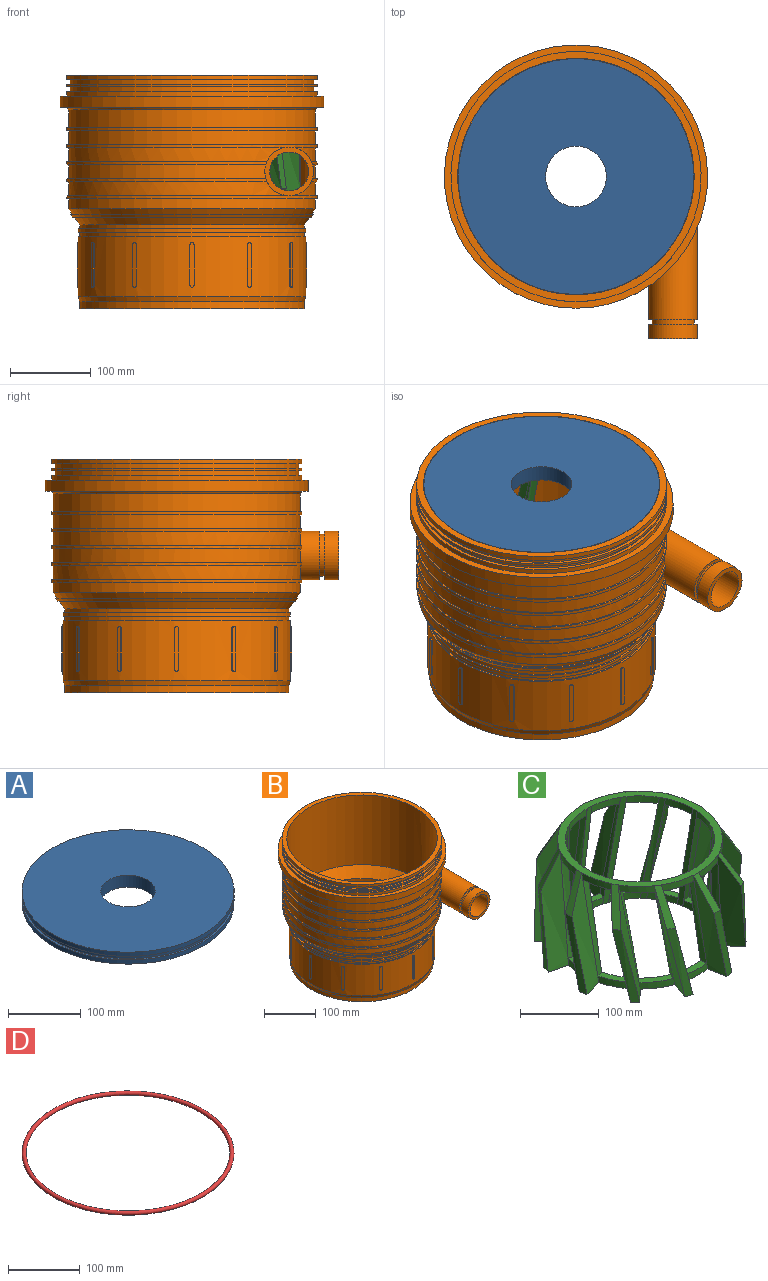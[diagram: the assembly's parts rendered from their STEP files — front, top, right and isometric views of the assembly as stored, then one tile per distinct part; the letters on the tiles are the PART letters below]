
ASSEMBLY  parts=4 mates=3
PART A: 8 faces, bbox 292x292x20 mm
  f0: cylinder r=146mm len=292mm, axis (0,0,-1), area 6421.4mm2, adj f1,f2
  f1: plane 292x292mm, normal (0,0,1), area 2723.8mm2, adj f0,f3
  f2: plane 292x292mm, normal (0,0,-1), area 62548.3mm2, adj f0,f7
  f3: cylinder r=143mm len=286mm, axis (0,0,-1), area 5391mm2, adj f1,f6
  f4: cylinder r=146mm len=292mm, axis (0,0,-1), area 6421.4mm2, adj f5,f6
  f5: plane 292x292mm, normal (0,0,1), area 62548.3mm2, adj f4,f7
  f6: plane 292x292mm, normal (0,0,-1), area 2723.8mm2, adj f3,f4
  f7: cylinder r=37.5mm len=75mm, axis (0,0,1), area 4712.4mm2, adj f2,f5
PART B: 122 faces, bbox 325x362.5x288.9 mm
  f0: plane 309x309mm, normal (0,0,-1), area 1735.4mm2, adj f1,f38,f116
  f1: cylinder r=154.5mm len=309mm, axis (0,0,1), area 3487.8mm2, adj f0,f2,f116
  f2: plane 309x309mm, normal (0,0,1), area 1719.7mm2, adj f1,f3,f116
  f3: cylinder r=152.5mm len=305mm, axis (0,0,1), area 14368.3mm2, adj f2,f4,f116
  f4: plane 309x309mm, normal (0,0,-1), area 1717.1mm2, adj f3,f5,f116
  f5: cylinder r=154.5mm len=309mm, axis (0,0,1), area 3481.9mm2, adj f4,f6,f116
  f6: plane 309x309mm, normal (0,0,1), area 1731.7mm2, adj f5,f39,f116
  f7: cylinder r=2.5mm len=5mm, axis (-1,0,0), area 12mm2, adj f8,f10,f11,f12
  f8: plane 50.15x1.52mm, normal (0,-1,0), area 76.3mm2, adj f7,f9,f11,f12
  f9: cylinder r=2.5mm len=5mm, axis (-1,0,0), area 12mm2, adj f8,f10,f11,f12
  f10: plane 50.15x1.52mm, normal (0,1,0), area 76.3mm2, adj f7,f9,f11,f12
  f11: plane 55.15x5mm, normal (-1,0,0), area 270.4mm2, adj f7,f8,f9,f10
  f12: cylinder r=140.5mm len=281mm, axis (0,0,1), area 62959mm2, adj f7,f8,f9,f10,f13,f14,f15,f16
  f13: cylinder r=2.5mm len=5.09mm, axis (-0.5,-0.87,0), area 12mm2, adj f12,f14,f16,f17
  f14: plane 50.15x1.32mm, normal (0.87,-0.5,0), area 76.3mm2, adj f12,f13,f15,f17
  f15: cylinder r=2.5mm len=5.09mm, axis (-0.5,-0.87,0), area 12mm2, adj f12,f14,f16,f17
  f16: plane 50.15x1.32mm, normal (-0.87,0.5,0), area 76.3mm2, adj f12,f13,f15,f17
  f17: plane 55.15x4.33mm, normal (-0.5,-0.87,0), area 270.4mm2, adj f13,f14,f15,f16
  f18: cylinder r=2.5mm len=5.09mm, axis (-0.87,-0.5,0), area 12mm2, adj f12,f19,f21,f22
  f19: plane 50.15x1.32mm, normal (0.5,-0.87,0), area 76.3mm2, adj f12,f18,f20,f22
  f20: cylinder r=2.5mm len=5.09mm, axis (-0.87,-0.5,0), area 12mm2, adj f12,f19,f21,f22
  f21: plane 50.15x1.32mm, normal (-0.5,0.87,0), area 76.3mm2, adj f12,f18,f20,f22
  f22: plane 55.15x4.33mm, normal (-0.87,-0.5,0), area 270.4mm2, adj f18,f19,f20,f21
  f23: plane 281x281mm, normal (0,0,1), area 1753mm2, adj f12,f24
  f24: cylinder r=138.5mm len=277mm, axis (0,0,1), area 4351.1mm2, adj f23,f25
  f25: plane 281x281mm, normal (0,0,-1), area 1753mm2, adj f24,f26
  f26: cylinder r=140.5mm len=281mm, axis (0,0,1), area 3531.2mm2, adj f25,f27
  f27: plane 281x281mm, normal (0,0,1), area 1753mm2, adj f26,f28
  f28: cylinder r=138.5mm len=277mm, axis (0,0,1), area 4136.4mm2, adj f27,f29
  f29: cone r=145.24mm half-angle=34.8deg, axis (0,0,1), area 10518.1mm2, adj f28,f30
  f30: plane 294.48x294.48mm, normal (0,0,-1), area 1837.7mm2, adj f29,f31
  f31: cone r=147.24mm half-angle=34.8deg, axis (0,0,1), area 3729.2mm2, adj f30,f32
  f32: plane 299.05x299.05mm, normal (0,0,1), area 1866.4mm2, adj f31,f33
  f33: cone r=152.5mm half-angle=34.8deg, axis (0,0,1), area 8211.2mm2, adj f32,f34
  f34: cylinder r=152.5mm len=305mm, axis (0,0,1), area 11498.2mm2, adj f33,f35
  f35: plane 309x309mm, normal (0,0,-1), area 1928.9mm2, adj f34,f36
  f36: cylinder r=154.5mm len=309mm, axis (0,0,1), area 3882.6mm2, adj f35,f37,f116
  f37: plane 309x309mm, normal (0,0,1), area 1914.4mm2, adj f36,f38,f116
  f38: cylinder r=152.5mm len=305mm, axis (0,0,1), area 15136.2mm2, adj f0,f37,f116
  f39: cylinder r=152.5mm len=305mm, axis (0,0,1), area 15067.7mm2, adj f6,f40,f116
  f40: plane 309x309mm, normal (0,0,-1), area 1881.5mm2, adj f39,f41,f116
  f41: cylinder r=154.5mm len=309mm, axis (0,0,1), area 3766.3mm2, adj f40,f42,f116
  f42: plane 309x309mm, normal (0,0,1), area 1928.9mm2, adj f41,f43
  f43: cylinder r=152.5mm len=305mm, axis (0,0,1), area 16289.2mm2, adj f42,f44
  f44: plane 309x309mm, normal (0,0,-1), area 1928.9mm2, adj f43,f45
  f45: cylinder r=154.5mm len=309mm, axis (0,0,1), area 3883mm2, adj f44,f46
  f46: plane 309x309mm, normal (0,0,1), area 1928.9mm2, adj f45,f47
  f47: cylinder r=152.5mm len=305mm, axis (0,0,1), area 21181.2mm2, adj f46,f48
  f48: cone r=154.5mm half-angle=33.7deg, axis (0,0,1), area 3477.4mm2, adj f47,f49
  f49: plane 325x325mm, normal (0,0,-1), area 7967.1mm2, adj f48,f50
  f50: cylinder r=162.5mm len=325mm, axis (0,0,1), area 14294.2mm2, adj f49,f51
  f51: plane 325x325mm, normal (0,0,1), area 7967.1mm2, adj f50,f52
  f52: cylinder r=154.5mm len=309mm, axis (0,0,1), area 5824.5mm2, adj f51,f53
  f53: plane 309x309mm, normal (0,0,1), area 3832.7mm2, adj f52,f54
  f54: cylinder r=150.5mm len=301mm, axis (0,0,1), area 5200.9mm2, adj f53,f55
  f55: plane 309x309mm, normal (0,0,-1), area 3832.7mm2, adj f54,f56
  f56: cylinder r=154.5mm len=309mm, axis (0,0,1), area 2912.3mm2, adj f55,f57
  f57: plane 309x309mm, normal (0,0,1), area 3832.7mm2, adj f56,f58
  f58: cylinder r=150.5mm len=301mm, axis (0,0,1), area 5200.9mm2, adj f57,f59
  f59: plane 309x309mm, normal (0,0,-1), area 3832.7mm2, adj f58,f60
  f60: cylinder r=154.5mm len=309mm, axis (0,0,1), area 5824.5mm2, adj f59,f61
  f61: plane 309x309mm, normal (0,0,1), area 8482.3mm2, adj f60,f62
  f62: cylinder r=145.5mm len=291mm, axis (0,0,1), area 147206.8mm2, adj f61,f63,f115
  f63: cone r=127.7mm half-angle=41.5deg, axis (0,0,1), area 23064.2mm2, adj f62,f64
  f64: cylinder r=127.7mm len=255.39mm, axis (0,0,1), area 11027.8mm2, adj f63,f65
  f65: plane 263.01x263.01mm, normal (0,0,-1), area 3100.8mm2, adj f64,f66
  f66: cylinder r=131.5mm len=263.01mm, axis (0,0,1), area 74363.3mm2, adj f65,f67
  f67: plane 277x277mm, normal (0,0,-1), area 5934.9mm2, adj f66,f68
  f68: cylinder r=138.5mm len=277mm, axis (0,0,1), area 7654.7mm2, adj f67,f69
  f69: cone r=140.5mm half-angle=17.9deg, axis (0,0,1), area 5717.9mm2, adj f12,f68
  f70: cylinder r=2.5mm len=5mm, axis (0,-1,0), area 11.9mm2, adj f12,f71,f73,f74
  f71: plane 50.15x1.52mm, normal (1,0,0), area 76.3mm2, adj f12,f70,f72,f74
  f72: cylinder r=2.5mm len=5mm, axis (0,-1,0), area 11.9mm2, adj f12,f71,f73,f74
  f73: plane 50.15x1.52mm, normal (-1,0,0), area 76.3mm2, adj f12,f70,f72,f74
  f74: plane 55.15x5mm, normal (0,-1,0), area 270.4mm2, adj f70,f71,f72,f73
  f75: cylinder r=2.5mm len=5.09mm, axis (0.87,-0.5,0), area 12mm2, adj f12,f76,f78,f79
  f76: plane 50.15x1.32mm, normal (0.5,0.87,0), area 76.3mm2, adj f12,f75,f77,f79
  f77: cylinder r=2.5mm len=5.09mm, axis (0.87,-0.5,0), area 12mm2, adj f12,f76,f78,f79
  f78: plane 50.15x1.32mm, normal (-0.5,-0.87,0), area 76.3mm2, adj f12,f75,f77,f79
  f79: plane 55.15x4.33mm, normal (0.87,-0.5,0), area 270.4mm2, adj f75,f76,f77,f78
  f80: cylinder r=2.5mm len=5.09mm, axis (0.5,-0.87,0), area 12mm2, adj f12,f81,f83,f84
  f81: plane 50.15x1.32mm, normal (0.87,0.5,0), area 76.3mm2, adj f12,f80,f82,f84
  f82: cylinder r=2.5mm len=5.09mm, axis (0.5,-0.87,0), area 12mm2, adj f12,f81,f83,f84
  f83: plane 50.15x1.32mm, normal (-0.87,-0.5,0), area 76.3mm2, adj f12,f80,f82,f84
  f84: plane 55.15x4.33mm, normal (0.5,-0.87,0), area 270.4mm2, adj f80,f81,f82,f83
  f85: cylinder r=2.5mm len=5mm, axis (1,0,0), area 12mm2, adj f12,f86,f88,f89
  f86: plane 50.15x1.52mm, normal (0,1,0), area 76.3mm2, adj f12,f85,f87,f89
  f87: cylinder r=2.5mm len=5mm, axis (1,0,0), area 12mm2, adj f12,f86,f88,f89
  f88: plane 50.15x1.52mm, normal (0,-1,0), area 76.3mm2, adj f12,f85,f87,f89
  f89: plane 55.15x5mm, normal (1,0,0), area 270.4mm2, adj f85,f86,f87,f88
  f90: cylinder r=2.5mm len=5.09mm, axis (-0.5,0.87,0), area 12mm2, adj f12,f91,f93,f94
  f91: plane 50.15x1.32mm, normal (-0.87,-0.5,0), area 76.3mm2, adj f12,f90,f92,f94
  f92: cylinder r=2.5mm len=5.09mm, axis (-0.5,0.87,0), area 12mm2, adj f12,f91,f93,f94
  f93: plane 50.15x1.32mm, normal (0.87,0.5,0), area 76.3mm2, adj f12,f90,f92,f94
  f94: plane 55.15x4.33mm, normal (-0.5,0.87,0), area 270.4mm2, adj f90,f91,f92,f93
  f95: cylinder r=2.5mm len=5.09mm, axis (0.87,0.5,0), area 12mm2, adj f12,f96,f98,f99
  f96: plane 50.15x1.32mm, normal (-0.5,0.87,0), area 76.3mm2, adj f12,f95,f97,f99
  f97: cylinder r=2.5mm len=5.09mm, axis (0.87,0.5,0), area 12mm2, adj f12,f96,f98,f99
  f98: plane 50.15x1.32mm, normal (0.5,-0.87,0), area 76.3mm2, adj f12,f95,f97,f99
  f99: plane 55.15x4.33mm, normal (0.87,0.5,0), area 270.4mm2, adj f95,f96,f97,f98
  f100: cylinder r=2.5mm len=5.09mm, axis (0.5,0.87,0), area 12mm2, adj f12,f101,f103,f104
  f101: plane 50.15x1.32mm, normal (-0.87,0.5,0), area 76.3mm2, adj f12,f100,f102,f104
  f102: cylinder r=2.5mm len=5.09mm, axis (0.5,0.87,0), area 12mm2, adj f12,f101,f103,f104
  f103: plane 50.15x1.32mm, normal (0.87,-0.5,0), area 76.3mm2, adj f12,f100,f102,f104
  f104: plane 55.15x4.33mm, normal (0.5,0.87,0), area 270.4mm2, adj f100,f101,f102,f103
  f105: cylinder r=2.5mm len=5.09mm, axis (-0.87,0.5,0), area 12mm2, adj f12,f106,f108,f109
  f106: plane 50.15x1.32mm, normal (-0.5,-0.87,0), area 76.3mm2, adj f12,f105,f107,f109
  f107: cylinder r=2.5mm len=5.09mm, axis (-0.87,0.5,0), area 12mm2, adj f12,f106,f108,f109
  f108: plane 50.15x1.32mm, normal (0.5,0.87,0), area 76.3mm2, adj f12,f105,f107,f109
  f109: plane 55.15x4.33mm, normal (-0.87,0.5,0), area 270.4mm2, adj f105,f106,f107,f108
  f110: cylinder r=2.5mm len=5mm, axis (0,1,0), area 12mm2, adj f12,f111,f113,f114
  f111: plane 50.15x1.52mm, normal (-1,0,0), area 76.3mm2, adj f12,f110,f112,f114
  f112: cylinder r=2.5mm len=5mm, axis (0,1,0), area 12mm2, adj f12,f111,f113,f114
  f113: plane 50.15x1.52mm, normal (1,0,0), area 76.3mm2, adj f12,f110,f112,f114
  f114: plane 55.15x5mm, normal (0,1,0), area 270.4mm2, adj f110,f111,f112,f113
  f115: cylinder r=24mm len=179.17mm, axis (0,1,0), area 18866.6mm2, adj f62,f121
  f116: cylinder r=30mm len=148.9mm, axis (0,1,0), area 16917.7mm2, adj f0,f1,f2,f3,f4,f5,f6,f36
  f117: plane 60x60mm, normal (0,-1,0), area 703.7mm2, adj f116,f118
  f118: cylinder r=26mm len=52mm, axis (0,1,0), area 914.8mm2, adj f117,f119
  f119: plane 60x60mm, normal (0,1,0), area 703.7mm2, adj f118,f120
  f120: cylinder r=30mm len=60mm, axis (0,1,0), area 3392.9mm2, adj f119,f121
  f121: plane 60x60mm, normal (0,-1,0), area 1017.9mm2, adj f115,f120
PART C: 158 faces, bbox 270x270x160 mm
  f0: cylinder r=105mm len=41.96mm, axis (0,0,-1), area 458.1mm2, adj f35,f36,f37,f48
  f1: cylinder r=105mm len=39.53mm, axis (0,0,-1), area 458.1mm2, adj f26,f36,f39,f46
  f2: cylinder r=105mm len=41.96mm, axis (0,0,-1), area 458.1mm2, adj f22,f36,f40,f41
  f3: cylinder r=105mm len=47.05mm, axis (0,0,-1), area 458.1mm2, adj f23,f36,f42,f43
  f4: cylinder r=105mm len=47.05mm, axis (0,0,-1), area 458.1mm2, adj f25,f36,f45,f50
  f5: cylinder r=105mm len=39.53mm, axis (0,0,-1), area 458.1mm2, adj f24,f36,f44,f47
  f6: cylinder r=105mm len=41.96mm, axis (0,0,-1), area 458.1mm2, adj f27,f36,f49,f52
  f7: cylinder r=105mm len=39.53mm, axis (0,0,-1), area 458.1mm2, adj f28,f36,f51,f54
  f8: cylinder r=105mm len=47.05mm, axis (0,0,-1), area 458.1mm2, adj f29,f36,f53,f56
  f9: cylinder r=105mm len=41.96mm, axis (0,0,-1), area 458.1mm2, adj f30,f36,f55,f58
  f10: cylinder r=105mm len=39.53mm, axis (0,0,-1), area 458.1mm2, adj f31,f36,f57,f60
  f11: cylinder r=95mm len=35.76mm, axis (0,0,-1), area 414.5mm2, adj f26,f36,f71,f72,f115,f117
  f12: cylinder r=95mm len=42.57mm, axis (0,0,-1), area 414.5mm2, adj f23,f36,f108,f109,f112,f114
  f13: cylinder r=95mm len=37.97mm, axis (0,0,-1), area 414.5mm2, adj f22,f36,f70,f72,f113,f114
  f14: cylinder r=95mm len=42.57mm, axis (0,0,-1), area 414.5mm2, adj f25,f36,f116,f117,f125,f127
  f15: cylinder r=95mm len=35.76mm, axis (0,0,-1), area 414.5mm2, adj f24,f36,f107,f109,f121,f124
  f16: cylinder r=95mm len=37.97mm, axis (0,0,-1), area 414.5mm2, adj f27,f36,f126,f127,f130,f134
  f17: cylinder r=95mm len=35.76mm, axis (0,0,-1), area 414.5mm2, adj f28,f36,f131,f134,f135,f137
  f18: cylinder r=95mm len=42.57mm, axis (0,0,-1), area 414.5mm2, adj f29,f36,f136,f137,f140,f142
  f19: cylinder r=95mm len=37.97mm, axis (0,0,-1), area 414.5mm2, adj f30,f36,f141,f142,f145,f147
  f20: cylinder r=95mm len=35.76mm, axis (0,0,-1), area 414.5mm2, adj f31,f36,f146,f147,f150,f152
  f21: cylinder r=95mm len=42.57mm, axis (0,0,-1), area 414.5mm2, adj f32,f36,f151,f152,f155,f157
  f22: plane 43.08x28.1mm, normal (0,0,1), area 436.3mm2, adj f2,f13,f40,f41,f70,f113
  f23: plane 45.37x13.65mm, normal (0,0,1), area 436.3mm2, adj f3,f12,f42,f43,f108,f112
  f24: plane 41.51x32mm, normal (0,0,1), area 436.3mm2, adj f5,f15,f44,f47,f107,f121
  f25: plane 45.37x13.65mm, normal (0,0,1), area 436.3mm2, adj f4,f14,f45,f50,f116,f125
  f26: plane 41.51x32mm, normal (0,0,1), area 436.3mm2, adj f1,f11,f39,f46,f71,f115
  f27: plane 43.08x28.1mm, normal (0,0,1), area 436.3mm2, adj f6,f16,f49,f52,f126,f130
  f28: plane 41.51x32mm, normal (0,0,1), area 436.3mm2, adj f7,f17,f51,f54,f131,f135
  f29: plane 45.37x13.65mm, normal (0,0,1), area 436.3mm2, adj f8,f18,f53,f56,f136,f140
  f30: plane 43.08x28.1mm, normal (0,0,1), area 436.3mm2, adj f9,f19,f55,f58,f141,f145
  f31: plane 41.51x32mm, normal (0,0,1), area 436.3mm2, adj f10,f20,f57,f60,f146,f150
  f32: plane 45.37x13.65mm, normal (0,0,1), area 436.3mm2, adj f21,f33,f38,f59,f151,f155
  f33: cylinder r=105mm len=47.05mm, axis (0,0,-1), area 458.1mm2, adj f32,f36,f38,f59
  f34: cylinder r=95mm len=37.97mm, axis (0,0,-1), area 414.5mm2, adj f35,f36,f120,f124,f156,f157
  f35: plane 43.08x28.1mm, normal (0,0,1), area 436.3mm2, adj f0,f34,f37,f48,f120,f156
  f36: plane 265.9x265.9mm, normal (0,0,-1), area 10053mm2, adj f0,f1,f2,f3,f4,f5,f6,f7
  f37: bspline ~160x34.94mm, area 4118.6mm2, adj f0,f35,f36,f61,f62,f63,f64,f65
  f38: bspline ~160x35.21mm, area 4126.9mm2, adj f32,f33,f36,f61,f62,f63,f79,f80
  f39: bspline ~160x42.96mm, area 4118.6mm2, adj f1,f26,f36,f61,f66,f67,f68,f69
  f40: bspline ~160x42.4mm, area 4126.9mm2, adj f2,f22,f36,f61,f66,f67,f70,f76
  f41: bspline ~160x34.94mm, area 4118.6mm2, adj f2,f22,f36,f61,f74,f75,f76,f77
  f42: bspline ~160x35.21mm, area 4126.9mm2, adj f3,f23,f36,f61,f74,f75,f104,f106
  f43: bspline ~160x40.32mm, area 4118.6mm2, adj f3,f23,f36,f61,f104,f106,f108,f110
  f44: bspline ~160x41.52mm, area 4126.9mm2, adj f5,f24,f36,f61,f97,f102,f107,f110
  f45: bspline ~160x40.32mm, area 4118.6mm2, adj f4,f25,f36,f61,f98,f100,f116,f118
  f46: bspline ~160x41.52mm, area 4126.9mm2, adj f1,f26,f36,f61,f68,f69,f115,f118
  f47: bspline ~160x42.96mm, area 4118.6mm2, adj f5,f24,f36,f61,f97,f102,f121,f122
  f48: bspline ~160x42.4mm, area 4126.9mm2, adj f0,f35,f36,f61,f64,f65,f120,f122
  f49: bspline ~160x34.94mm, area 4118.6mm2, adj f6,f27,f36,f61,f91,f96,f126,f128
  f50: bspline ~160x35.21mm, area 4126.9mm2, adj f4,f25,f36,f61,f98,f100,f125,f128
  f51: bspline ~160x42.96mm, area 4118.6mm2, adj f7,f28,f36,f61,f92,f94,f131,f132
  f52: bspline ~160x42.4mm, area 4126.9mm2, adj f6,f27,f36,f61,f91,f96,f130,f132
  f53: bspline ~160x40.32mm, area 4118.6mm2, adj f8,f29,f36,f61,f88,f89,f136,f138
  f54: bspline ~160x41.52mm, area 4126.9mm2, adj f7,f28,f36,f61,f92,f94,f135,f138
  f55: bspline ~160x34.94mm, area 4118.6mm2, adj f9,f30,f36,f61,f85,f86,f141,f143
  f56: bspline ~160x35.21mm, area 4126.9mm2, adj f8,f29,f36,f61,f88,f89,f140,f143
  f57: bspline ~160x42.96mm, area 4118.6mm2, adj f10,f31,f36,f61,f82,f83,f146,f148
  f58: bspline ~160x42.4mm, area 4126.9mm2, adj f9,f30,f36,f61,f85,f86,f145,f148
  f59: bspline ~160x40.32mm, area 4118.6mm2, adj f32,f33,f36,f61,f79,f80,f151,f153
  f60: bspline ~160x41.52mm, area 4126.9mm2, adj f10,f31,f36,f61,f82,f83,f150,f153
  f61: plane 210.89x210.89mm, normal (0,0,1), area 6343.1mm2, adj f37,f38,f39,f40,f41,f42,f43,f44
  f62: bspline ~110.53x35.82mm, area 1293.9mm2, adj f36,f37,f38,f63
  f63: bspline ~49.5x28.96mm, area 574.6mm2, adj f37,f38,f61,f62
  f64: cylinder r=105mm len=45.91mm, axis (0,0,1), area 458.1mm2, adj f37,f48,f61,f65
  f65: plane 44.37x19.55mm, normal (0,0,-1), area 436.3mm2, adj f37,f48,f64,f99,f120,f156
  f66: bspline ~160x38.41mm, area 1293.9mm2, adj f36,f39,f40,f67
  f67: bspline ~49.48x33.96mm, area 574.6mm2, adj f39,f40,f61,f66
  f68: cylinder r=105mm len=34.48mm, axis (0,0,1), area 458.1mm2, adj f39,f46,f61,f69
  f69: plane 38.15x36.85mm, normal (0,0,-1), area 436.3mm2, adj f39,f46,f68,f71,f101,f115
  f70: bspline ~160x27.34mm, area 1410.9mm2, adj f13,f22,f40,f72,f73,f77
  f71: bspline ~160x26.75mm, area 1410.9mm2, adj f11,f26,f39,f69,f72,f101
  f72: bspline ~160x27.03mm, area 1319mm2, adj f11,f13,f36,f61,f70,f71
  f73: cylinder r=95mm len=41.54mm, axis (0,0,1), area 414.5mm2, adj f61,f70,f77,f113
  f74: bspline ~110.53x35.82mm, area 1293.9mm2, adj f36,f41,f42,f75
  f75: bspline ~49.5x28.96mm, area 574.6mm2, adj f41,f42,f61,f74
  f76: cylinder r=105mm len=45.91mm, axis (0,0,1), area 458.1mm2, adj f40,f41,f61,f77
  f77: plane 44.37x19.55mm, normal (0,0,-1), area 436.3mm2, adj f40,f41,f70,f73,f76,f113
  f78: cylinder r=95mm len=40.76mm, axis (0,0,1), area 414.5mm2, adj f61,f80,f151,f155
  f79: cylinder r=105mm len=45.05mm, axis (0,0,1), area 458.1mm2, adj f38,f59,f61,f80
  f80: plane 44.27x21.7mm, normal (0,0,-1), area 436.3mm2, adj f38,f59,f78,f79,f151,f155
  f81: cylinder r=95mm len=31.19mm, axis (0,0,1), area 414.5mm2, adj f61,f83,f146,f150
  f82: cylinder r=105mm len=34.48mm, axis (0,0,1), area 458.1mm2, adj f57,f60,f61,f83
  f83: plane 38.15x36.85mm, normal (0,0,-1), area 436.3mm2, adj f57,f60,f81,f82,f146,f150
  f84: cylinder r=95mm len=41.54mm, axis (0,0,1), area 414.5mm2, adj f61,f86,f141,f145
  f85: cylinder r=105mm len=45.91mm, axis (0,0,1), area 458.1mm2, adj f55,f58,f61,f86
  f86: plane 44.37x19.55mm, normal (0,0,-1), area 436.3mm2, adj f55,f58,f84,f85,f141,f145
  f87: cylinder r=95mm len=40.76mm, axis (0,0,1), area 414.5mm2, adj f61,f89,f136,f140
  f88: cylinder r=105mm len=45.05mm, axis (0,0,1), area 458.1mm2, adj f53,f56,f61,f89
  f89: plane 44.27x21.7mm, normal (0,0,-1), area 436.3mm2, adj f53,f56,f87,f88,f136,f140
  f90: cylinder r=95mm len=31.19mm, axis (0,0,1), area 414.5mm2, adj f61,f94,f131,f135
  f91: plane 44.37x19.55mm, normal (0,0,-1), area 436.3mm2, adj f49,f52,f93,f96,f126,f130
  f92: cylinder r=105mm len=34.48mm, axis (0,0,1), area 458.1mm2, adj f51,f54,f61,f94
  f93: cylinder r=95mm len=41.54mm, axis (0,0,1), area 414.5mm2, adj f61,f91,f126,f130
  f94: plane 38.15x36.85mm, normal (0,0,-1), area 436.3mm2, adj f51,f54,f90,f92,f131,f135
  f95: cylinder r=95mm len=40.76mm, axis (0,0,1), area 414.5mm2, adj f61,f98,f116,f125
  f96: cylinder r=105mm len=45.91mm, axis (0,0,1), area 458.1mm2, adj f49,f52,f61,f91
  f97: cylinder r=105mm len=34.48mm, axis (0,0,1), area 458.1mm2, adj f44,f47,f61,f102
  f98: plane 44.27x21.7mm, normal (0,0,-1), area 436.3mm2, adj f45,f50,f95,f100,f116,f125
  f99: cylinder r=95mm len=41.54mm, axis (0,0,1), area 414.5mm2, adj f61,f65,f120,f156
  f100: cylinder r=105mm len=45.05mm, axis (0,0,1), area 458.1mm2, adj f45,f50,f61,f98
  f101: cylinder r=95mm len=31.19mm, axis (0,0,1), area 414.5mm2, adj f61,f69,f71,f115
  f102: plane 38.15x36.85mm, normal (0,0,-1), area 436.3mm2, adj f44,f47,f97,f105,f107,f121
  f103: cylinder r=95mm len=40.76mm, axis (0,0,1), area 414.5mm2, adj f61,f106,f108,f112
  f104: cylinder r=105mm len=45.05mm, axis (0,0,1), area 458.1mm2, adj f42,f43,f61,f106
  f105: cylinder r=95mm len=31.19mm, axis (0,0,1), area 414.5mm2, adj f61,f102,f107,f121
  f106: plane 44.27x21.7mm, normal (0,0,-1), area 436.3mm2, adj f42,f43,f103,f104,f108,f112
  f107: bspline ~160x27.73mm, area 1410.9mm2, adj f15,f24,f44,f102,f105,f109
  f108: bspline ~160x27.91mm, area 1410.9mm2, adj f12,f23,f43,f103,f106,f109
  f109: bspline ~160x29.9mm, area 1319mm2, adj f12,f15,f36,f61,f107,f108
  f110: bspline ~110.53x32.83mm, area 1293.9mm2, adj f36,f43,f44,f111
  f111: bspline ~49.48x34.43mm, area 574.6mm2, adj f43,f44,f61,f110
  f112: bspline ~160x27.38mm, area 1410.9mm2, adj f12,f23,f42,f103,f106,f114
  f113: bspline ~160x27.18mm, area 1410.9mm2, adj f13,f22,f41,f73,f77,f114
  f114: bspline ~160x32.87mm, area 1319mm2, adj f12,f13,f36,f61,f112,f113
  f115: bspline ~160x27.73mm, area 1410.9mm2, adj f11,f26,f46,f69,f101,f117
  f116: bspline ~160x27.91mm, area 1410.9mm2, adj f14,f25,f45,f95,f98,f117
  f117: bspline ~160x29.9mm, area 1319mm2, adj f11,f14,f36,f61,f115,f116
  f118: bspline ~110.53x32.83mm, area 1293.9mm2, adj f36,f45,f46,f119
  f119: bspline ~49.48x34.43mm, area 574.6mm2, adj f45,f46,f61,f118
  f120: bspline ~160x27.34mm, area 1410.9mm2, adj f34,f35,f48,f65,f99,f124
  f121: bspline ~160x26.75mm, area 1410.9mm2, adj f15,f24,f47,f102,f105,f124
  f122: bspline ~160x38.41mm, area 1293.9mm2, adj f36,f47,f48,f123
  f123: bspline ~49.48x33.96mm, area 574.6mm2, adj f47,f48,f61,f122
  f124: bspline ~160x27.03mm, area 1319mm2, adj f15,f34,f36,f61,f120,f121
  f125: bspline ~160x27.38mm, area 1410.9mm2, adj f14,f25,f50,f95,f98,f127
  f126: bspline ~160x27.18mm, area 1410.9mm2, adj f16,f27,f49,f91,f93,f127
  f127: bspline ~160x32.87mm, area 1319mm2, adj f14,f16,f36,f61,f125,f126
  f128: bspline ~110.53x35.82mm, area 1293.9mm2, adj f36,f49,f50,f129
  f129: bspline ~49.5x28.96mm, area 574.6mm2, adj f49,f50,f61,f128
  f130: bspline ~160x27.34mm, area 1410.9mm2, adj f16,f27,f52,f91,f93,f134
  f131: bspline ~160x26.75mm, area 1410.9mm2, adj f17,f28,f51,f90,f94,f134
  f132: bspline ~160x38.41mm, area 1293.9mm2, adj f36,f51,f52,f133
  f133: bspline ~49.48x33.96mm, area 574.6mm2, adj f51,f52,f61,f132
  f134: bspline ~160x27.03mm, area 1319mm2, adj f16,f17,f36,f61,f130,f131
  f135: bspline ~160x27.73mm, area 1410.9mm2, adj f17,f28,f54,f90,f94,f137
  f136: bspline ~160x27.91mm, area 1410.9mm2, adj f18,f29,f53,f87,f89,f137
  f137: bspline ~160x29.9mm, area 1319mm2, adj f17,f18,f36,f61,f135,f136
  f138: bspline ~110.53x32.83mm, area 1293.9mm2, adj f36,f53,f54,f139
  f139: bspline ~49.48x34.43mm, area 574.6mm2, adj f53,f54,f61,f138
  f140: bspline ~160x27.38mm, area 1410.9mm2, adj f18,f29,f56,f87,f89,f142
  f141: bspline ~160x27.18mm, area 1410.9mm2, adj f19,f30,f55,f84,f86,f142
  f142: bspline ~160x32.87mm, area 1319mm2, adj f18,f19,f36,f61,f140,f141
  f143: bspline ~110.53x35.82mm, area 1293.9mm2, adj f36,f55,f56,f144
  f144: bspline ~49.5x28.96mm, area 574.6mm2, adj f55,f56,f61,f143
  f145: bspline ~160x27.34mm, area 1410.9mm2, adj f19,f30,f58,f84,f86,f147
  f146: bspline ~160x26.75mm, area 1410.9mm2, adj f20,f31,f57,f81,f83,f147
  f147: bspline ~160x27.03mm, area 1319mm2, adj f19,f20,f36,f61,f145,f146
  f148: bspline ~160x38.41mm, area 1293.9mm2, adj f36,f57,f58,f149
  f149: bspline ~49.48x33.96mm, area 574.6mm2, adj f57,f58,f61,f148
  f150: bspline ~160x27.73mm, area 1410.9mm2, adj f20,f31,f60,f81,f83,f152
  f151: bspline ~160x27.91mm, area 1410.9mm2, adj f21,f32,f59,f78,f80,f152
  f152: bspline ~160x29.9mm, area 1319mm2, adj f20,f21,f36,f61,f150,f151
  f153: bspline ~110.53x32.83mm, area 1293.9mm2, adj f36,f59,f60,f154
  f154: bspline ~49.48x34.43mm, area 574.6mm2, adj f59,f60,f61,f153
  f155: bspline ~160x27.38mm, area 1410.9mm2, adj f21,f32,f38,f78,f80,f157
  f156: bspline ~160x27.18mm, area 1410.9mm2, adj f34,f35,f37,f65,f99,f157
  f157: bspline ~160x32.87mm, area 1319mm2, adj f21,f34,f36,f61,f155,f156
PART D: 1 faces, bbox 320x320x6 mm
  f0: torus R=144.83mm, axis (0,0,-1), area 17153mm2
PLACE A rot(axis=(1,0,0),180deg) t=(-22.1,-8.21,365.11)mm
PLACE B t=(-22.1,-8.21,46.03)mm
PLACE C rot(axis=(1,0,0),180deg) t=(-22.1,-8.21,-24.89)mm
PLACE D t=(-22.1,-8.21,-78.08)mm
MATE fastened A.f0 <-> D.f0  axis (0,0,1) through (-22.1,-8.21,155.11)mm
MATE fastened B.f1 <-> A.f0  axis (0,0,1) through (-22.1,-8.21,165.11)mm
MATE revolute C.f0 <-> A.f0  axis (0,0,1) through (-22.1,-8.21,135.11)mm
